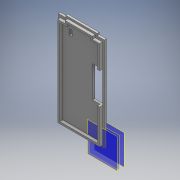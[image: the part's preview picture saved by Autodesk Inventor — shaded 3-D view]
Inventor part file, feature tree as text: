
AUTODESK INVENTOR PART (.ipt)
format: ipt  version: 2016 SP1 (Build 200210100, 210)  size: 173,056 bytes
history: native  units: mm
features: other x7, extrude x4, sketch x4
ambient origin geometry x8: Origin, YZ Plane, XZ Plane, XY Plane, X Axis, Y Axis, Z Axis, Center Point
bodies: Body1 (feature_tree)
feature tree (15):
  other  "Bryła1"
  other  "Płaszczyzna konstrukcyjna1"
  extrude  "Wyciągnięcie proste19"  Depth=1.5mm
  other  "Płaszczyzna konstrukcyjna3"
  extrude  "Wyciągnięcie proste20"  Depth=1.5mm
  other  "Płaszczyzna konstrukcyjna2"
  other  "Płaszczyzna konstrukcyjna5"
  other  "Płaszczyzna konstrukcyjna6"
  other  "Płaszczyzna konstrukcyjna4"
  extrude  "Wyciągnięcie proste24"  Depth=1.5mm
  extrude  "Wyciągnięcie proste26"  Depth=1.5mm
  sketch  "Szkic21"
  sketch  "Szkic22"
  sketch  "Szkic26"
  sketch  "Szkic28"
